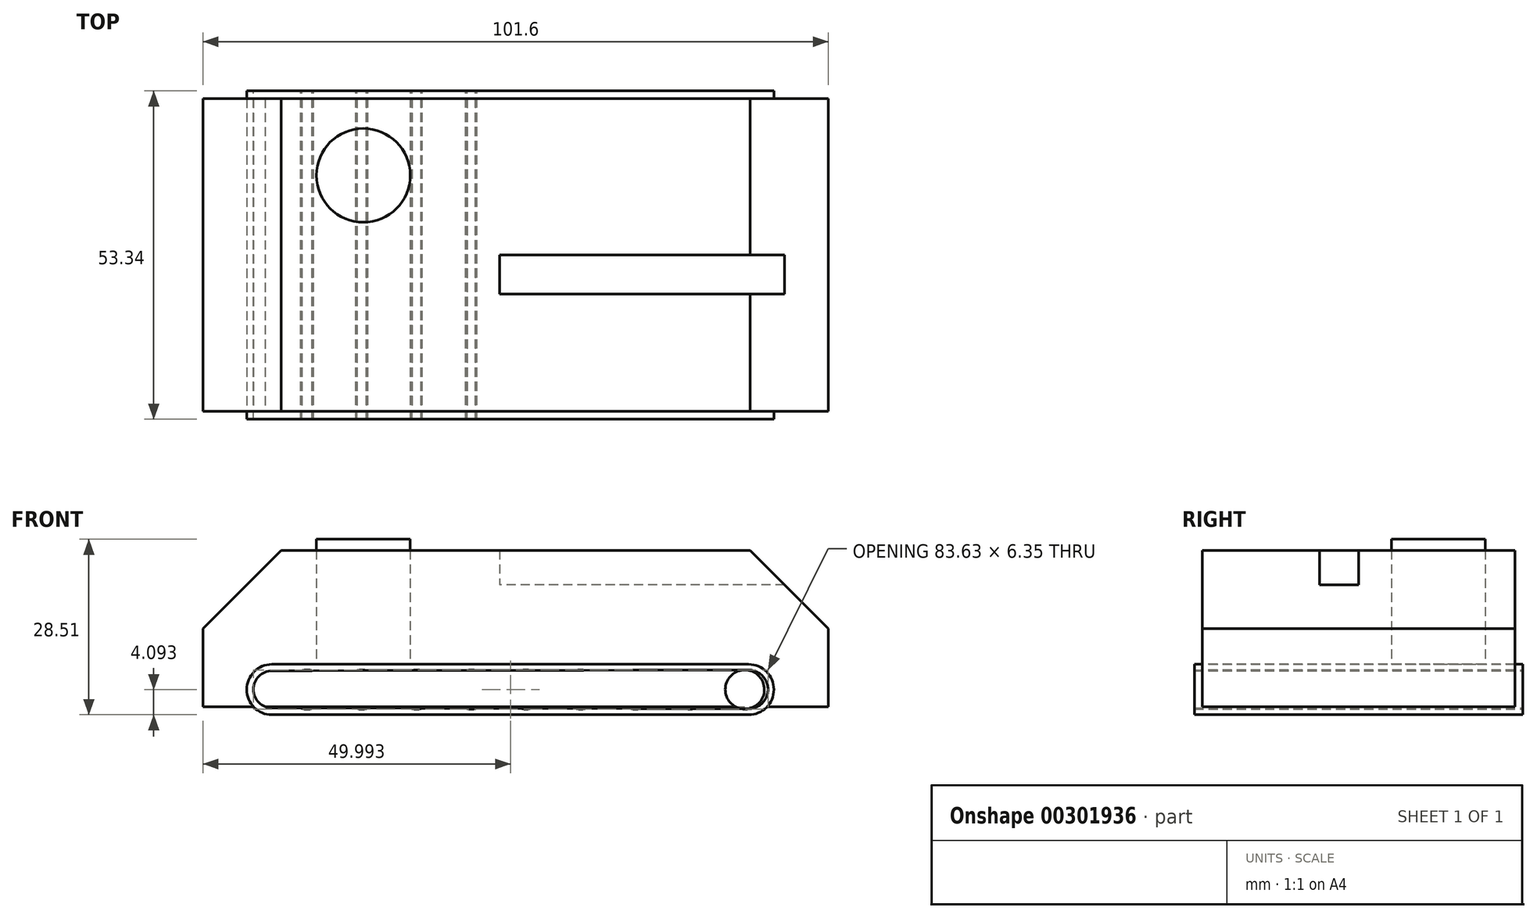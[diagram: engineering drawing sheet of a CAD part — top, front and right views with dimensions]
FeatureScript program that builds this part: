
annotation { "Feature Type Name" : "Feature", "Feature Type Description" : "" }
export const myFeature = defineFeature(function(context is Context, id is Id, definition is map)
    precondition{}
    {
        {
            var Q0;
            Q0=qCreatedBy(makeId("Front.planeOp"),FACE);
            var sketch = newSketch(context, id + "F0", { "sketchPlane" : qUnion([Q0])});
            skLineSegment(sketch, "E0.bottom", {"start": v(-48.2, 18.53) * mm, "end": v(53.4, 18.53) * mm});
            skLineSegment(sketch, "E0.top", {"start": v(-48.2, -6.87) * mm, "end": v(53.4, -6.87) * mm});
            skLineSegment(sketch, "E0.left", {"start": v(-48.2, 18.53) * mm, "end": v(-48.2, -6.87) * mm});
            skLineSegment(sketch, "E0.right", {"start": v(53.4, 18.53) * mm, "end": v(53.4, -6.87) * mm});
            skSolve(sketch);
        }
        {
            var Q0;
            Q0 = qSketchRegion(id + "F0", true);
            extrude(context, id + "F1", {"entities" : qUnion([Q0]), "endBound" : BoundingType.SYMMETRIC, "depth" : 50.8 * mm});
        }
        {
            var Q0;
            Q0=makeQuery(id+"F1.opExtrude","SWEPT_EDGE",EDGE,{"disambiguationData":[OSD([sQuery(id+"F0.wireOp",EDGE,"E0.bottom"),sQuery(id+"F0.wireOp",EDGE,"E0.right")])]});
            chamfer(context, id + "F2", {"entities" : qUnion([Q0]), "width" : 12.7 * mm, "tangentPropagation" : true});
        }
        {
            var Q0;
            {var subQ0=sQuery(id+"F0.wireOp",EDGE,"E0.bottom");var subQ1=sQuery(id+"F0.wireOp",EDGE,"E0.left");Q0=makeQuery(id+"FcVe9WIwIIqOok3_1.boolean.opBoolean","SPLIT",EDGE,{"disambiguationData":[TD([makeQuery(id+"FcVe9WIwIIqOok3_1.opExtrude","SWEPT_FACE",FACE,{"disambiguationData":[OSD([sQuery(id+"FFeugXQvQEomX8z_1.wireOp",EDGE,"HdgW5Uxv-r3Z2-OHHn-IWJb-arqK4aW7sNmA.right")])]})])],"derivedFrom":makeQuery(id+"F1.opExtrude","SWEPT_EDGE",EDGE,{"disambiguationData":[OSD([subQ0,subQ1])]})});}
            var Q1;
            {var subQ0=sQuery(id+"F0.wireOp",EDGE,"E0.bottom");var subQ1=sQuery(id+"F0.wireOp",EDGE,"E0.left");Q1=makeQuery(id+"FcVe9WIwIIqOok3_1.boolean.opBoolean","SPLIT",EDGE,{"disambiguationData":[TD([makeQuery(id+"FcVe9WIwIIqOok3_1.opExtrude","SWEPT_FACE",FACE,{"disambiguationData":[OSD([sQuery(id+"FFeugXQvQEomX8z_1.wireOp",EDGE,"HdgW5Uxv-r3Z2-OHHn-IWJb-arqK4aW7sNmA.left")])]})])],"derivedFrom":makeQuery(id+"F1.opExtrude","SWEPT_EDGE",EDGE,{"disambiguationData":[OSD([subQ0,subQ1])]})});}
            chamfer(context, id + "F3", {"entities" : qUnion([Q0, Q1]), "width" : 12.7 * mm, "tangentPropagation" : true});
        }
        {
            var Q0;
            Q0=qCreatedBy(makeId("Front.planeOp"),FACE);
            var sketch = newSketch(context, id + "F4", { "sketchPlane" : qUnion([Q0])});
            skLineSegment(sketch, "E1", {"start": v(-37, 0) * mm, "end": v(40.45, 0) * mm});
            skLineSegment(sketch, "E2", {"start": v(-37, -8.2) * mm, "end": v(40.45, -8.2) * mm});
            skArc(sketch, "E3", {"start": v(-37, 0) * mm, "mid": v(-41.1, -4.1) * mm, "end": v(-37, -8.2) * mm});
            skArc(sketch, "E4", {"start": v(40.45, -8.2) * mm, "mid": v(44.54, -4.1) * mm, "end": v(40.45, 0) * mm});
            skCircle(sketch, "E5", {"center": v(-31.3, -4.1) * mm, "radius": 3.17 * mm});
            skCircle(sketch, "E6", {"center": v(-22.4, -4.1) * mm, "radius": 3.18 * mm});
            skCircle(sketch, "E7", {"center": v(-13.51, -4.1) * mm, "radius": 3.18 * mm});
            skCircle(sketch, "E8", {"center": v(-4.62, -4.1) * mm, "radius": 3.18 * mm});
            skCircle(sketch, "E9", {"center": v(4.27, -4.1) * mm, "radius": 3.18 * mm});
            skCircle(sketch, "E10", {"center": v(13.16, -4.1) * mm, "radius": 3.18 * mm});
            skCircle(sketch, "E11", {"center": v(22.05, -4.1) * mm, "radius": 3.18 * mm});
            skCircle(sketch, "E12", {"center": v(30.94, -4.1) * mm, "radius": 3.18 * mm});
            skCircle(sketch, "E13", {"center": v(39.83, -4.1) * mm, "radius": 3.18 * mm});
            skLineSegment(sketch, "E14", {"start": v(-37, -1.04) * mm, "end": v(40.45, -0.92) * mm});
            skLineSegment(sketch, "E15", {"start": v(-37, -7.1) * mm, "end": v(40.45, -7.21) * mm});
            skArc(sketch, "E16", {"start": v(-37, -1.04) * mm, "mid": v(-40.03, -4.07) * mm, "end": v(-37, -7.1) * mm});
            skArc(sketch, "E17", {"start": v(40.45, -7.21) * mm, "mid": v(43.6, -4.07) * mm, "end": v(40.45, -0.92) * mm});
            skSolve(sketch);
        }
        {
            var Q0;
            Q0 = qSketchRegion(id + "F4", true);
            extrude(context, id + "F5", {"entities" : qUnion([Q0]), "operationType" : NewBodyOperationType.REMOVE, "endBound" : BoundingType.SYMMETRIC, "oppositeDirection" : true, "depth" : 152.4 * mm});
        }
        {
            var Q0;
            Q0 = qSketchRegion(id + "F4", true);
            extrude(context, id + "F6", {"entities" : qUnion([Q0]), "endBound" : BoundingType.SYMMETRIC, "depth" : 53.34 * mm});
        }
        {
            var Q0;
            {var subQ0=sQuery(id+"F4.wireOp",EDGE,"E14");var subQ1=sQuery(id+"F4.wireOp",EDGE,"E7");var subQ2=makeQuery(id+"F4.imprint","INTERSECT",VERTEX,{"disambiguationData":[OD(0.0)],"derivedFrom":[subQ1,subQ0]});Q0=makeQuery(id+"F4.imprint","IMPRINT",FACE,{"disambiguationData":[TD([[makeQuery(id+"F4.imprint","IMPRINT",EDGE,{"disambiguationData":[TD([[subQ2,-1.0]])],"derivedFrom":subQ1}),1.0]])]});}
            var Q1;
            {var subQ0=sQuery(id+"F4.wireOp",EDGE,"E14");var subQ1=sQuery(id+"F4.wireOp",EDGE,"E6");var subQ2=makeQuery(id+"F4.imprint","INTERSECT",VERTEX,{"disambiguationData":[OD(0.0)],"derivedFrom":[subQ1,subQ0]});Q1=makeQuery(id+"F4.imprint","IMPRINT",FACE,{"disambiguationData":[TD([[makeQuery(id+"F4.imprint","IMPRINT",EDGE,{"disambiguationData":[TD([[subQ2,-1.0]])],"derivedFrom":subQ1}),1.0]])]});}
            var Q2;
            {var subQ0=sQuery(id+"F4.wireOp",EDGE,"E14");var subQ1=sQuery(id+"F4.wireOp",EDGE,"E5");var subQ2=makeQuery(id+"F4.imprint","INTERSECT",VERTEX,{"disambiguationData":[OD(0.0)],"derivedFrom":[subQ1,subQ0]});Q2=makeQuery(id+"F4.imprint","IMPRINT",FACE,{"disambiguationData":[TD([[makeQuery(id+"F4.imprint","IMPRINT",EDGE,{"disambiguationData":[TD([[subQ2,-1.0]])],"derivedFrom":subQ1}),1.0]])]});}
            var Q3;
            {var subQ0=sQuery(id+"F4.wireOp",EDGE,"E14");var subQ1=sQuery(id+"F4.wireOp",EDGE,"E8");var subQ2=makeQuery(id+"F4.imprint","INTERSECT",VERTEX,{"disambiguationData":[OD(0.0)],"derivedFrom":[subQ1,subQ0]});Q3=makeQuery(id+"F4.imprint","IMPRINT",FACE,{"disambiguationData":[TD([[makeQuery(id+"F4.imprint","IMPRINT",EDGE,{"disambiguationData":[TD([[subQ2,-1.0]])],"derivedFrom":subQ1}),1.0]])]});}
            var Q4;
            {var subQ0=sQuery(id+"F4.wireOp",EDGE,"E14");var subQ1=sQuery(id+"F4.wireOp",EDGE,"E9");var subQ2=makeQuery(id+"F4.imprint","INTERSECT",VERTEX,{"disambiguationData":[OD(0.0)],"derivedFrom":[subQ1,subQ0]});Q4=makeQuery(id+"F4.imprint","IMPRINT",FACE,{"disambiguationData":[TD([[makeQuery(id+"F4.imprint","IMPRINT",EDGE,{"disambiguationData":[TD([[subQ2,-1.0]])],"derivedFrom":subQ1}),1.0]])]});}
            var Q5;
            {var subQ0=sQuery(id+"F4.wireOp",EDGE,"E14");var subQ1=sQuery(id+"F4.wireOp",EDGE,"E10");var subQ2=makeQuery(id+"F4.imprint","INTERSECT",VERTEX,{"disambiguationData":[OD(0.0)],"derivedFrom":[subQ1,subQ0]});Q5=makeQuery(id+"F4.imprint","IMPRINT",FACE,{"disambiguationData":[TD([[makeQuery(id+"F4.imprint","IMPRINT",EDGE,{"disambiguationData":[TD([[subQ2,-1.0]])],"derivedFrom":subQ1}),1.0]])]});}
            var Q6;
            {var subQ0=sQuery(id+"F4.wireOp",EDGE,"E14");var subQ1=sQuery(id+"F4.wireOp",EDGE,"E11");var subQ2=makeQuery(id+"F4.imprint","INTERSECT",VERTEX,{"disambiguationData":[OD(0.0)],"derivedFrom":[subQ1,subQ0]});Q6=makeQuery(id+"F4.imprint","IMPRINT",FACE,{"disambiguationData":[TD([[makeQuery(id+"F4.imprint","IMPRINT",EDGE,{"disambiguationData":[TD([[subQ2,-1.0]])],"derivedFrom":subQ1}),1.0]])]});}
            var Q7;
            {var subQ0=sQuery(id+"F4.wireOp",EDGE,"E14");var subQ1=sQuery(id+"F4.wireOp",EDGE,"E12");var subQ2=makeQuery(id+"F4.imprint","INTERSECT",VERTEX,{"disambiguationData":[OD(0.0)],"derivedFrom":[subQ1,subQ0]});Q7=makeQuery(id+"F4.imprint","IMPRINT",FACE,{"disambiguationData":[TD([[makeQuery(id+"F4.imprint","IMPRINT",EDGE,{"disambiguationData":[TD([[subQ2,-1.0]])],"derivedFrom":subQ1}),1.0]])]});}
            var Q8;
            {var subQ0=sQuery(id+"F4.wireOp",EDGE,"E15");var subQ1=sQuery(id+"F4.wireOp",EDGE,"E13");var subQ2=makeQuery(id+"F4.imprint","INTERSECT",VERTEX,{"derivedFrom":[subQ1,subQ0]});Q8=makeQuery(id+"F4.imprint","IMPRINT",FACE,{"disambiguationData":[TD([[makeQuery(id+"F4.imprint","IMPRINT",EDGE,{"disambiguationData":[TD([[subQ2,1.0]])],"derivedFrom":subQ1}),1.0]])]});}
            extrude(context, id + "F7", {"entities" : qUnion([Q0, Q1, Q2, Q3, Q4, Q5, Q6, Q7, Q8]), "endBound" : BoundingType.SYMMETRIC, "depth" : 53.34 * mm});
        }
        {
            var Q0;
            Q0=qCreatedBy(makeId("Top.planeOp"),FACE);
            var sketch = newSketch(context, id + "F8", { "sketchPlane" : qUnion([Q0])});
            skCircle(sketch, "E18", {"center": v(-22.16, 12.95) * mm, "radius": 7.62 * mm});
            skSolve(sketch);
        }
        {
            var Q0;
            Q0 = qSketchRegion(id + "F8", true);
            extrude(context, id + "F9", {"entities" : qUnion([Q0]), "depth" : 20.32 * mm});
        }
        {
            var Q0;
            Q0=qCreatedBy(makeId("Right.planeOp"),FACE);
            var sketch = newSketch(context, id + "F10", { "sketchPlane" : qUnion([Q0])});
            skLineSegment(sketch, "E19.bottom", {"start": v(0, 19.27) * mm, "end": v(-6.35, 19.27) * mm});
            skLineSegment(sketch, "E19.top", {"start": v(0, 12.92) * mm, "end": v(-6.35, 12.92) * mm});
            skLineSegment(sketch, "E19.left", {"start": v(0, 19.27) * mm, "end": v(0, 12.92) * mm});
            skLineSegment(sketch, "E19.right", {"start": v(-6.35, 19.27) * mm, "end": v(-6.35, 12.92) * mm});
            skSolve(sketch);
        }
        {
            var Q0;
            Q0 = qSketchRegion(id + "F10", true);
            extrude(context, id + "F11", {"entities" : qUnion([Q0]), "operationType" : NewBodyOperationType.REMOVE, "depth" : 50.8 * mm});
        }
    });
